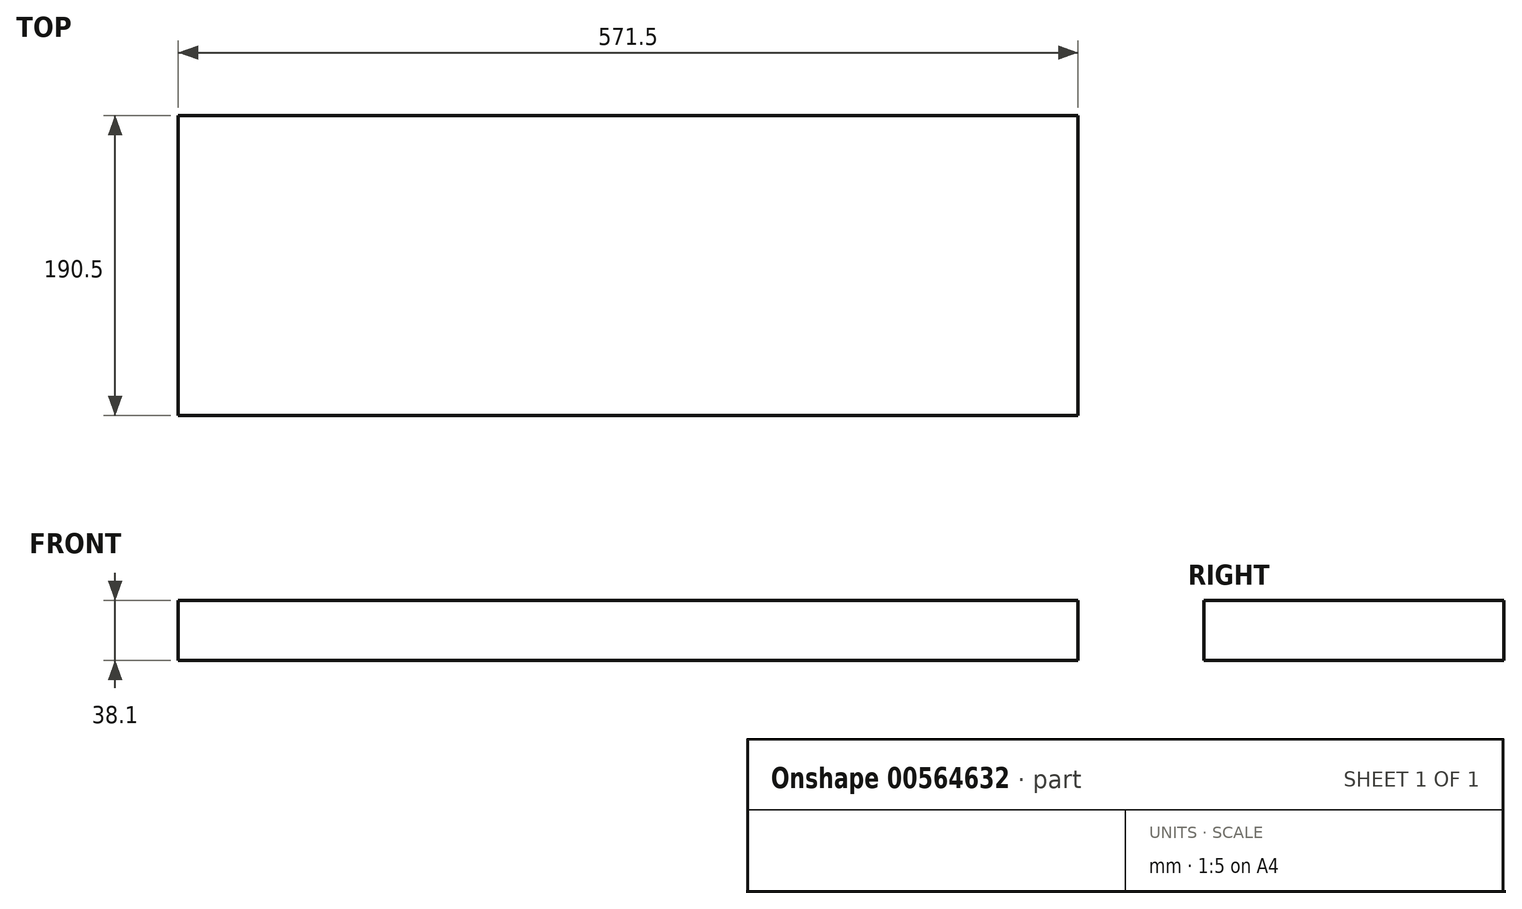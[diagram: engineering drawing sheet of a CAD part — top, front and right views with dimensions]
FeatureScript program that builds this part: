
annotation { "Feature Type Name" : "Feature", "Feature Type Description" : "" }
export const myFeature = defineFeature(function(context is Context, id is Id, definition is map)
    precondition{}
    {
        {
            var Q0;
            Q0=qCreatedBy(makeId("Top.planeOp"),FACE);
            var sketch = newSketch(context, id + "F0", { "sketchPlane" : qUnion([Q0])});
            skLineSegment(sketch, "E0.bottom", {"start": v(-285.75, 95.25) * mm, "end": v(285.75, 95.25) * mm});
            skLineSegment(sketch, "E0.top", {"start": v(-285.75, -95.25) * mm, "end": v(285.75, -95.25) * mm});
            skLineSegment(sketch, "E0.left", {"start": v(-285.75, 95.25) * mm, "end": v(-285.75, -95.25) * mm});
            skLineSegment(sketch, "E0.right", {"start": v(285.75, 95.25) * mm, "end": v(285.75, -95.25) * mm});
            skPoint(sketch, "E0.middle", {"position": v(0, 0) * mm});
            skSolve(sketch);
        }
        {
            var Q0;
            Q0=makeQuery(id+"F0.imprint","IMPRINT",FACE,{"disambiguationData":[TD([[makeQuery(id+"F0.imprint","IMPRINT",EDGE,{"derivedFrom":sQuery(id+"F0.wireOp",EDGE,"E0.bottom")}),-1.0]])]});
            extrude(context, id + "F1", {"entities" : qUnion([Q0]), "depth" : 38.1 * mm, "offsetDistance" : 25.4 * mm});
        }
    });
